# Revit family: PRD_FrankeWS_PwrSpplUnts_PowerSupply_ACEX9001
name_source: partatom
category: Electrical Equipment
revit_build: Autodesk Revit 2018 (Build: 20190510_1515(x64)
units: mm (PartAtom-declared; Revit-internal decimal feet)

## family parameters
Always vertical = No
Cut with Voids When Loaded = No
OmniClass Number = 23.45.55.11
OmniClass Title = Sanitary Components
Part Type = Transformer
Room Calculation Point = No
Round Connector Dimension = Use Diameter
Shared = No
Work Plane-Based = Yes

## types (2) — shared parameters
AssetType = Fixed
BIMObjectName = PRD_AR_PowerSupplyUnits_PowerSupply_ACEX9001
Category = Pr_60_70, Power supply products
Communication = no
Compatible A3000 = no
Default Elevation = 1219 mm
Description = Mains unit, for central power supply, operating voltage 100-240 V AC, output voltage switchable between 7 V DC, 31.5 W or 12 V DC, 50 W.
DurationUnit = year
GrossWeight = 0.51 kg
IP_Code = IP20
IfcExportAs = IfcTransformerType
IfcExportType = NOTDEFINED
Manufacturer = KWC Group AG
ManufacturerName = KWC Group AG
ManufacturerURL = www.kwc.com
MaximumCableLength = 10 m
Model = ACEX9001
ModelNumber = 2030039477
ModelReference = ACEX9001
NBSDescription = Power supply products
NBSReference = 90-70-05/390
Name = Power supply ACEX9001
NetWeight = 0.49 kg
NominalDepth = 69 mm  [stored 0.226378 ft]
NominalHeight = 95 mm
NominalWidth = 109 mm  [stored 0.357612 ft]
PowerSupplyMaterial = PRD_AR_SyntheticGrey
PowerSwitch = no
PrimaryApparentPower = 50 VA
PrimaryCurrent = 0 A
PrimaryFrequency = 50 Hz
PrimaryVoltage = 240 V
ProductInformation = https://pim.kwc.com
SecondaryApparentPower = 0 VA
SecondaryCurrent = 0 A
SecondaryCurrentType = DC
SecondaryFrequency = 0 Hz
Size = 69 x 95 x 109 mm
URL = www.kwc.com
Uniclass2015Code = Pr_60_70
Uniclass2015Title = Power supply products
Uniclass2015Version = Products v1.10
Version = 1
Voltage = 240
WarrantyDurationUnit = year

## per-type parameters (varying)
| type | MaximumApparentPower | SecondaryVoltage |
| ACEX9001 - 12V DC, 50.0W | 50 VA | 12 V |
| ACEX9001 - 7V DC, 31.5W | 32 VA | 7 V |

note: [stored X ft] marks values corroborated as IEEE doubles in the binary element streams (Revit-internal decimal feet)

## geometry (parser evidence)
native form markers: Sweep x2
no freeform markers — native parametric forms only
